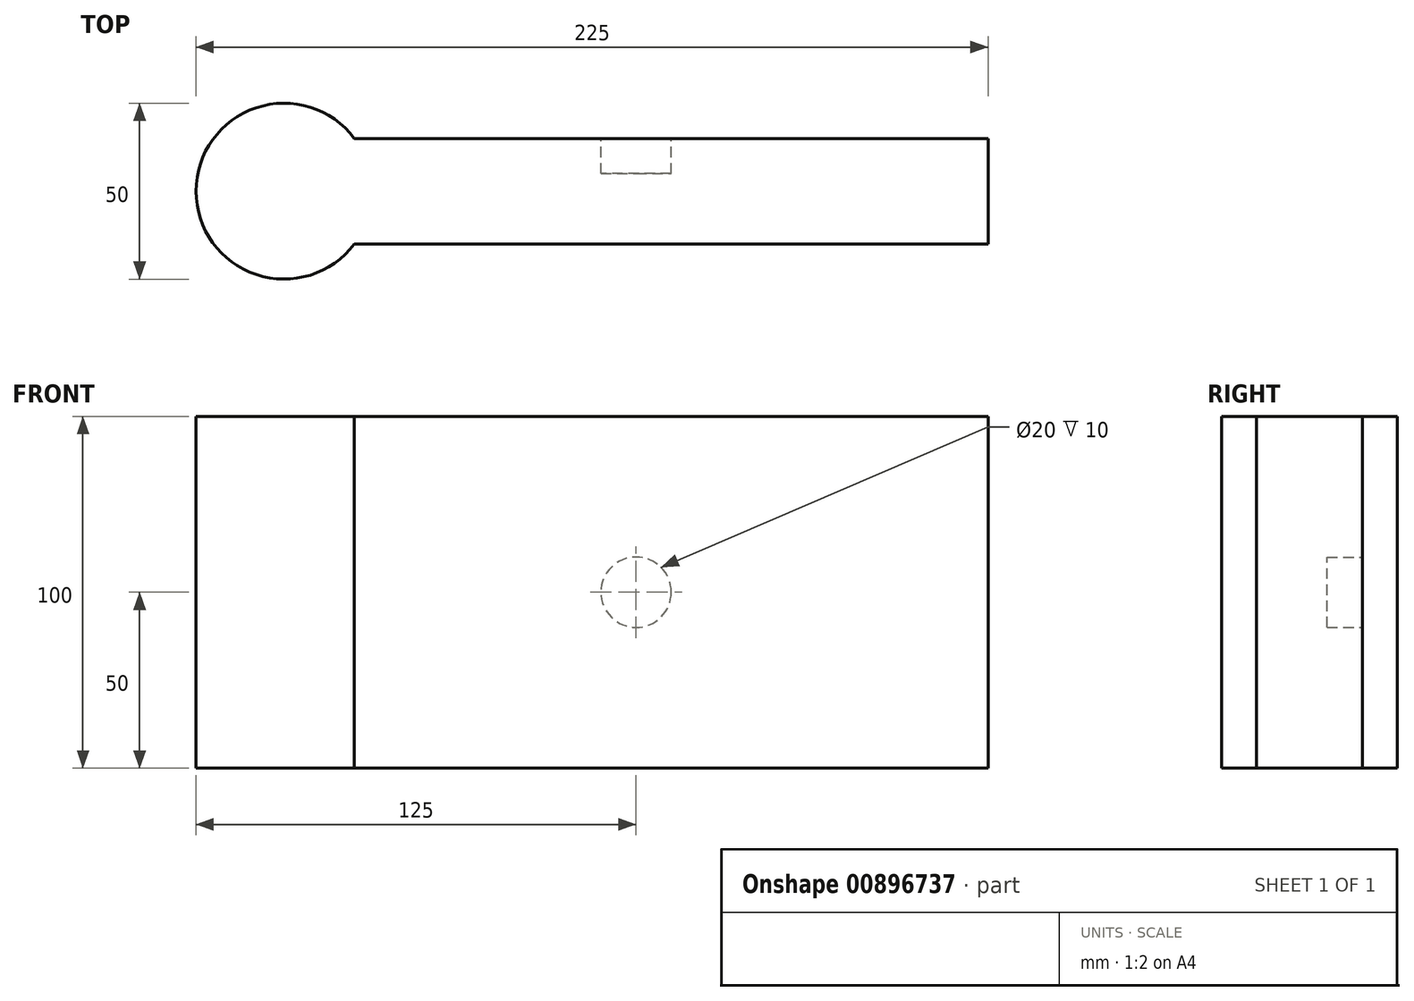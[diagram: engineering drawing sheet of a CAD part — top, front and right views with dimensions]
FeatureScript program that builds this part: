
annotation { "Feature Type Name" : "Feature", "Feature Type Description" : "" }
export const myFeature = defineFeature(function(context is Context, id is Id, definition is map)
    precondition{}
    {
        {
            var Q0;
            Q0=qCreatedBy(makeId("Front.planeOp"),FACE);
            var sketch = newSketch(context, id + "F0", { "sketchPlane" : qUnion([Q0])});
            skLineSegment(sketch, "E0.bottom", {"start": v(-100, 50) * mm, "end": v(100, 50) * mm});
            skLineSegment(sketch, "E0.top", {"start": v(-100, -50) * mm, "end": v(100, -50) * mm});
            skLineSegment(sketch, "E0.left", {"start": v(-100, 50) * mm, "end": v(-100, -50) * mm});
            skLineSegment(sketch, "E0.right", {"start": v(100, 50) * mm, "end": v(100, -50) * mm});
            skPoint(sketch, "E0.middle", {"position": v(0, 0) * mm});
            skSolve(sketch);
        }
        {
            var Q0;
            Q0=makeQuery(id+"F0.imprint","IMPRINT",FACE,{"disambiguationData":[TD([[makeQuery(id+"F0.imprint","IMPRINT",EDGE,{"derivedFrom":sQuery(id+"F0.wireOp",EDGE,"E0.bottom")}),-1.0]])]});
            extrude(context, id + "F1", {"entities" : qUnion([Q0]), "depth" : 30 * mm, "offsetDistance" : 25 * mm});
        }
        {
            var Q0;
            Q0=qCreatedBy(makeId("Top.planeOp"),FACE);
            var sketch = newSketch(context, id + "F2", { "sketchPlane" : qUnion([Q0])});
            skLineSegment(sketch, "E1", {"start": v(0, 32.13) * mm, "end": v(0, -63.38) * mm, "construction": true});
            skCircle(sketch, "E2", {"center": v(-100, -15) * mm, "radius": 25 * mm});
            skCircle(sketch, "E3.MirrorC", {"center": v(100, -15) * mm, "radius": 25 * mm});
            skSolve(sketch);
        }
        {
            var Q0;
            Q0=makeQuery(id+"F2.imprint","IMPRINT",FACE,{"disambiguationData":[TD([[makeQuery(id+"F2.imprint","IMPRINT",EDGE,{"derivedFrom":sQuery(id+"F2.wireOp",EDGE,"E2")}),1.0]])]});
            var Q1;
            Q1=makeQuery(id+"F2.imprint","IMPRINT",FACE,{"disambiguationData":[TD([[makeQuery(id+"F2.imprint","IMPRINT",EDGE,{"derivedFrom":sQuery(id+"F2.wireOp",EDGE,"E3.MirrorC")}),-1.0]])]});
            extrude(context, id + "F3", {"entities" : qUnion([Q0, Q1]), "operationType" : NewBodyOperationType.ADD, "endBound" : BoundingType.SYMMETRIC, "depth" : 100 * mm, "offsetDistance" : 25 * mm});
        }
        {
            var Q0;
            Q0=qCreatedBy(makeId("Front.planeOp"),FACE);
            var sketch = newSketch(context, id + "F4", { "sketchPlane" : qUnion([Q0])});
            skCircle(sketch, "E4", {"center": v(0, 0) * mm, "radius": 10 * mm});
            skSolve(sketch);
        }
        {
            var Q0;
            Q0=makeQuery(id+"F4.imprint","IMPRINT",FACE,{"disambiguationData":[TD([[makeQuery(id+"F4.imprint","IMPRINT",EDGE,{"derivedFrom":sQuery(id+"F4.wireOp",EDGE,"E4")}),1.0]])]});
            extrude(context, id + "F5", {"entities" : qUnion([Q0]), "operationType" : NewBodyOperationType.REMOVE, "depth" : 10 * mm, "offsetDistance" : 25 * mm});
        }
    });
